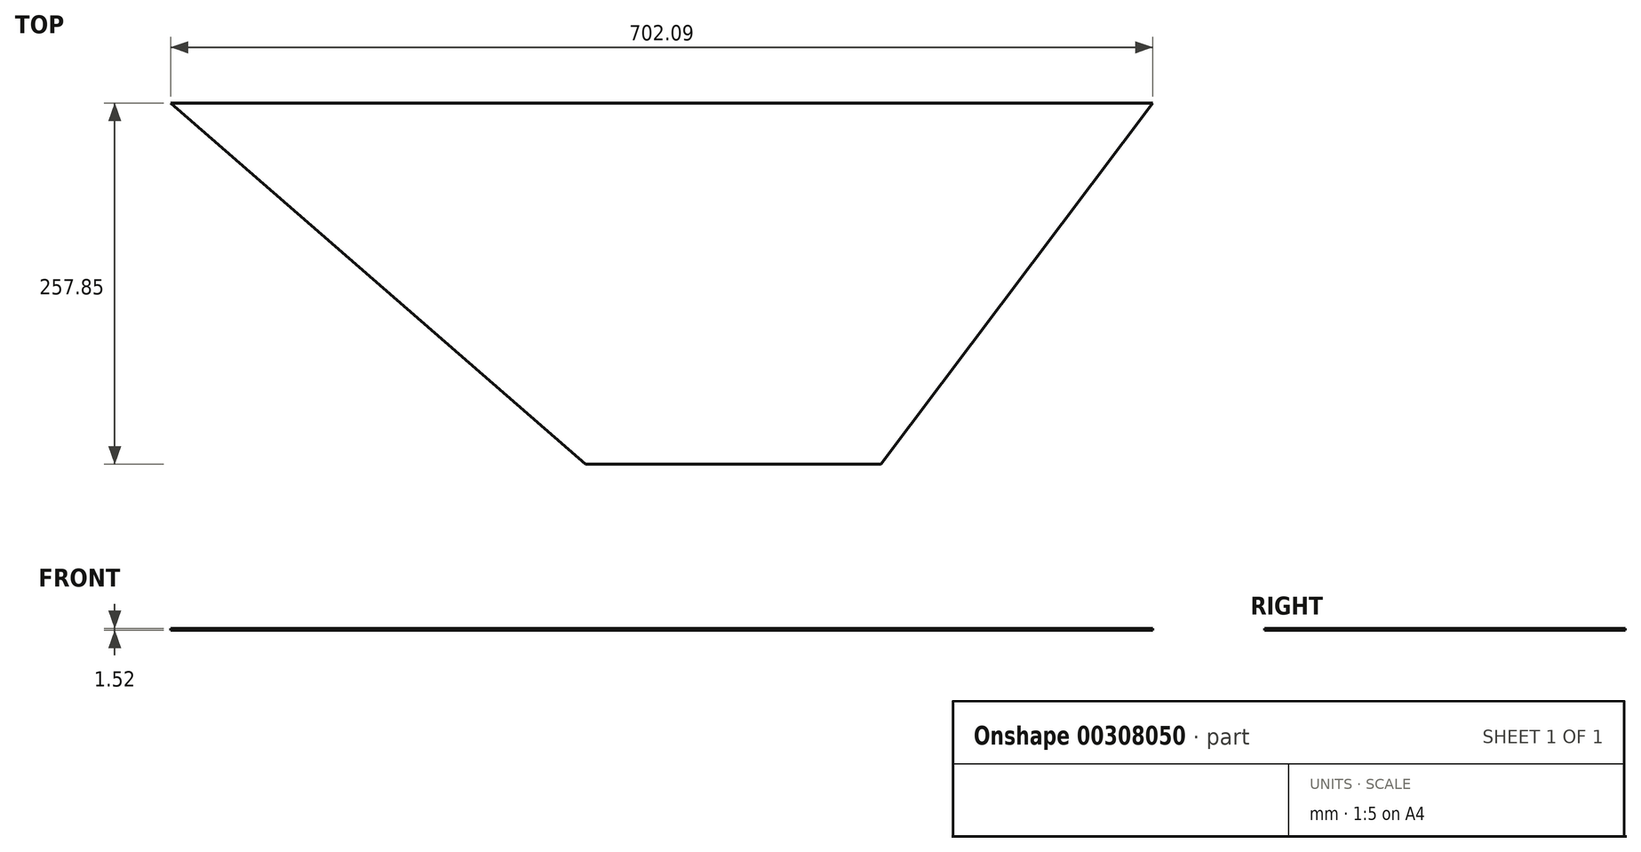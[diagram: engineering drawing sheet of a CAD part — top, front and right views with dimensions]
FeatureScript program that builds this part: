
annotation { "Feature Type Name" : "Feature", "Feature Type Description" : "" }
export const myFeature = defineFeature(function(context is Context, id is Id, definition is map)
    precondition{}
    {
        {
            var Q0;
            Q0=qCreatedBy(makeId("Top.planeOp"), FACE);
            var sketch = newSketch(context, id + "F0", { "sketchPlane" : qUnion([Q0])});
            skLineSegment(sketch, "E0", {"start": v(-66.1, -162.86) * mm, "end": v(145.05, -162.86) * mm});
            skLineSegment(sketch, "E1", {"start": v(145.05, -162.86) * mm, "end": v(339.36, 95) * mm});
            skLineSegment(sketch, "E2", {"start": v(-362.73, 95) * mm, "end": v(-66.1, -162.86) * mm});
            skLineSegment(sketch, "E3", {"start": v(-362.73, 95) * mm, "end": v(339.36, 95) * mm});
            skLineSegment(sketch, "E4", {"start": v(-97.25, -135.79) * mm, "end": v(166.07, -134.97) * mm});
            skLineSegment(sketch, "E5.0", {"start": v(-330.18, 66.7) * mm, "end": v(319.55, 68.7) * mm});
            skSolve(sketch);
        }
        {
            var Q0;
            Q0 = qSketchRegion(id + "F0", true);
            extrude(context, id + "F1", {"entities" : qUnion([Q0]), "depth" : 1.52 * mm, "offsetDistance" : 25.4 * mm});
        }
    });
